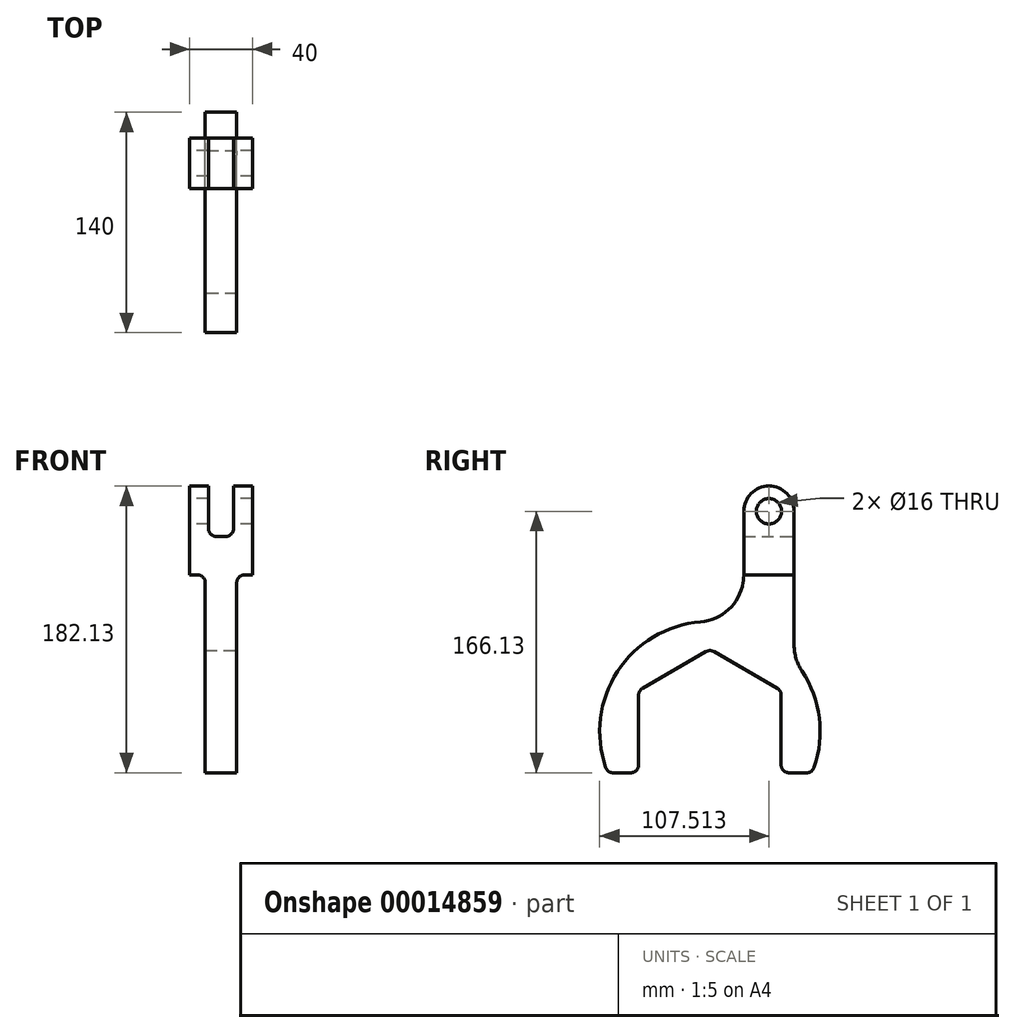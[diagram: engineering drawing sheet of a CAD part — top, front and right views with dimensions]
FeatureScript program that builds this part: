
annotation { "Feature Type Name" : "Feature", "Feature Type Description" : "" }
export const myFeature = defineFeature(function(context is Context, id is Id, definition is map)
    precondition{}
    {
        {
            var Q0;
            Q0=qCreatedBy(makeId("Right.planeOp"),FACE);
            var sketch = newSketch(context, id + "F0", { "sketchPlane" : qUnion([Q0])});
            skCircle(sketch, "E0.cCircle", {"center": v(0, 0) * mm, "radius": 45.25 * mm, "construction": true});
            skLineSegment(sketch, "E0.0", {"start": v(-45.25, -26.13) * mm, "end": v(-45.25, 26.13) * mm});
            skLineSegment(sketch, "E0.1", {"start": v(-45.25, 26.13) * mm, "end": v(0, 52.25) * mm});
            skLineSegment(sketch, "E0.2", {"start": v(0, 52.25) * mm, "end": v(45.25, 26.13) * mm});
            skLineSegment(sketch, "E0.3", {"start": v(45.25, 26.13) * mm, "end": v(45.25, -26.13) * mm});
            skLineSegment(sketch, "E0.4", {"start": v(22.63, -39.19) * mm, "end": v(21.51, -39.83) * mm});
            skPoint(sketch, "E0.0.midPoint", {"position": v(-45.25, 0) * mm});
            skLineSegment(sketch, "E1", {"start": v(0, 0) * mm, "end": v(0, 140) * mm, "construction": true});
            skLineSegment(sketch, "E2", {"start": v(0, 140) * mm, "end": v(132.53, 140) * mm, "construction": true});
            skLineSegment(sketch, "E3", {"start": v(0, 0) * mm, "end": v(37.51, 140) * mm, "construction": true});
            skCircle(sketch, "E4", {"center": v(37.51, 140) * mm, "radius": 8 * mm});
            skArc(sketch, "E5", {"start": v(53.51, 140) * mm, "mid": v(37.51, 156) * mm, "end": v(21.51, 140) * mm});
            skLineSegment(sketch, "E6", {"start": v(53.51, 140) * mm, "end": v(53.51, 55) * mm});
            skArc(sketch, "E7", {"start": v(64.94, -26.13) * mm, "mid": v(69.65, 6.99) * mm, "end": v(58.46, 38.5) * mm});
            skLineSegment(sketch, "E8", {"start": v(37.51, 140) * mm, "end": v(37.51, 210.9) * mm, "construction": true});
            skLineSegment(sketch, "E9.0.MirrorCS", {"start": v(21.51, 140) * mm, "end": v(21.51, 99.64) * mm});
            skLineSegment(sketch, "E10", {"start": v(-64.94, -26.13) * mm, "end": v(-45.25, -26.13) * mm});
            skPoint(sketch, "E11.orphan", {"position": v(53.51, -53.76) * mm});
            skArc(sketch, "E12.trimOffspring", {"start": v(-5.94, 69.75) * mm, "mid": v(-59.62, 36.69) * mm, "end": v(-64.94, -26.13) * mm});
            skPoint(sketch, "E13.orphan", {"position": v(-113.23, -26.13) * mm});
            skLineSegment(sketch, "E14.trimOffspring", {"start": v(45.25, -26.13) * mm, "end": v(64.94, -26.13) * mm});
            skPoint(sketch, "E15.visualSharp", {"position": v(53.51, 45.13) * mm});
            skArc(sketch, "E15.filletArc", {"start": v(53.51, 55) * mm, "mid": v(54.78, 46.4) * mm, "end": v(58.46, 38.5) * mm});
            skPoint(sketch, "E16.newPointA", {"position": v(21.51, -53.76) * mm});
            skArc(sketch, "E16.filletArc", {"start": v(-5.94, 69.75) * mm, "mid": v(13.6, 79.35) * mm, "end": v(21.51, 99.64) * mm});
            skSolve(sketch);
        }
        {
            var Q0;
            Q0=qSketchRegion(id+"F0",true);
            extrude(context, id + "F1", {"entities" : qUnion([Q0]), "endBound" : BoundingType.SYMMETRIC, "depth" : 40 * mm});
        }
        {
            var Q0;
            Q0=makeQuery(id+"F1.opExtrude","CAP_FACE",FACE,{"disambiguationData":[OSD([sQuery(id+"F0.wireOp",EDGE,"E0.0"),sQuery(id+"F0.wireOp",EDGE,"E0.1"),sQuery(id+"F0.wireOp",EDGE,"E0.2"),sQuery(id+"F0.wireOp",EDGE,"E0.3"),sQuery(id+"F0.wireOp",EDGE,"E4"),sQuery(id+"F0.wireOp",EDGE,"E5"),sQuery(id+"F0.wireOp",EDGE,"E6"),sQuery(id+"F0.wireOp",EDGE,"E7"),sQuery(id+"F0.wireOp",EDGE,"E9.0.MirrorCS"),sQuery(id+"F0.wireOp",EDGE,"E10"),sQuery(id+"F0.wireOp",EDGE,"E12.trimOffspring"),sQuery(id+"F0.wireOp",EDGE,"E14.trimOffspring"),sQuery(id+"F0.wireOp",EDGE,"E15.filletArc"),sQuery(id+"F0.wireOp",EDGE,"E16.filletArc")])],"isStart":false});
            var sketch = newSketch(context, id + "F2", { "sketchPlane" : qUnion([Q0])});
            skArc(sketch, "E17.0", {"start": v(-5.94, 69.75) * mm, "mid": v(-59.62, 36.69) * mm, "end": v(-64.94, -26.13) * mm});
            skLineSegment(sketch, "E18.0", {"start": v(-64.94, -26.13) * mm, "end": v(-45.25, -26.13) * mm});
            skLineSegment(sketch, "E19.0", {"start": v(-45.25, -26.13) * mm, "end": v(-45.25, 26.13) * mm});
            skLineSegment(sketch, "E20.0", {"start": v(-45.25, 26.13) * mm, "end": v(0, 52.25) * mm});
            skLineSegment(sketch, "E21.0", {"start": v(0, 52.25) * mm, "end": v(45.25, 26.13) * mm});
            skLineSegment(sketch, "E22.0", {"start": v(45.25, 26.13) * mm, "end": v(45.25, -26.13) * mm});
            skLineSegment(sketch, "E23.0", {"start": v(45.25, -26.13) * mm, "end": v(64.94, -26.13) * mm});
            skArc(sketch, "E24.0", {"start": v(64.94, -26.13) * mm, "mid": v(69.65, 6.99) * mm, "end": v(58.46, 38.5) * mm});
            skArc(sketch, "E25.0", {"start": v(53.51, 55) * mm, "mid": v(54.78, 46.4) * mm, "end": v(58.46, 38.5) * mm});
            skArc(sketch, "E26.0", {"start": v(-5.94, 69.75) * mm, "mid": v(13.6, 79.35) * mm, "end": v(21.51, 99.64) * mm});
            skLineSegment(sketch, "E27.0", {"start": v(53.51, 140) * mm, "end": v(53.51, 55) * mm});
            skLineSegment(sketch, "E28", {"start": v(21.51, 99.64) * mm, "end": v(67.54, 99.64) * mm});
            skSolve(sketch);
        }
        {
            var Q0;
            Q0=qSketchRegion(id+"F2",true);
            extrude(context, id + "F3", {"entities" : qUnion([Q0]), "operationType" : NewBodyOperationType.REMOVE, "oppositeDirection" : true, "depth" : 10 * mm});
        }
        {
            var Q0;
            Q0=makeQuery(id+"F1.opExtrude","CAP_FACE",FACE,{"disambiguationData":[OSD([sQuery(id+"F0.wireOp",EDGE,"E0.0"),sQuery(id+"F0.wireOp",EDGE,"E0.1"),sQuery(id+"F0.wireOp",EDGE,"E0.2"),sQuery(id+"F0.wireOp",EDGE,"E0.3"),sQuery(id+"F0.wireOp",EDGE,"E4"),sQuery(id+"F0.wireOp",EDGE,"E5"),sQuery(id+"F0.wireOp",EDGE,"E6"),sQuery(id+"F0.wireOp",EDGE,"E7"),sQuery(id+"F0.wireOp",EDGE,"E9.0.MirrorCS"),sQuery(id+"F0.wireOp",EDGE,"E10"),sQuery(id+"F0.wireOp",EDGE,"E12.trimOffspring"),sQuery(id+"F0.wireOp",EDGE,"E14.trimOffspring"),sQuery(id+"F0.wireOp",EDGE,"E15.filletArc"),sQuery(id+"F0.wireOp",EDGE,"E16.filletArc")])],"isStart":true});
            var sketch = newSketch(context, id + "F4", { "sketchPlane" : qUnion([Q0])});
            skArc(sketch, "E29.0", {"start": v(5.94, 69.75) * mm, "mid": v(-13.6, 79.35) * mm, "end": v(-21.51, 99.64) * mm});
            skLineSegment(sketch, "E30.0", {"start": v(-21.51, 99.64) * mm, "end": v(-53.51, 99.64) * mm});
            skLineSegment(sketch, "E31.0", {"start": v(-53.51, 140) * mm, "end": v(-53.51, 55) * mm});
            skArc(sketch, "E32.0", {"start": v(-53.51, 55) * mm, "mid": v(-54.78, 46.4) * mm, "end": v(-58.46, 38.5) * mm});
            skArc(sketch, "E33.0", {"start": v(-64.94, -26.13) * mm, "mid": v(-69.65, 6.99) * mm, "end": v(-58.46, 38.5) * mm});
            skLineSegment(sketch, "E34.0", {"start": v(-45.25, -26.13) * mm, "end": v(-64.94, -26.13) * mm});
            skLineSegment(sketch, "E35.0", {"start": v(-45.25, 26.13) * mm, "end": v(-45.25, -26.13) * mm});
            skLineSegment(sketch, "E36.0", {"start": v(0, 52.25) * mm, "end": v(-45.25, 26.13) * mm});
            skLineSegment(sketch, "E37.0", {"start": v(45.25, 26.13) * mm, "end": v(0, 52.25) * mm});
            skLineSegment(sketch, "E38.0", {"start": v(45.25, -26.13) * mm, "end": v(45.25, 26.13) * mm});
            skLineSegment(sketch, "E39.0", {"start": v(64.94, -26.13) * mm, "end": v(45.25, -26.13) * mm});
            skArc(sketch, "E40.0", {"start": v(5.94, 69.75) * mm, "mid": v(59.62, 36.69) * mm, "end": v(64.94, -26.13) * mm});
            skSolve(sketch);
        }
        {
            var Q0;
            Q0=qSketchRegion(id+"F4",true);
            extrude(context, id + "F5", {"entities" : qUnion([Q0]), "operationType" : NewBodyOperationType.REMOVE, "oppositeDirection" : true, "depth" : 10 * mm});
        }
        {
            var Q0;
            Q0=makeQuery(id+"F5.boolean.opBoolean","COPY",EDGE,{"derivedFrom":makeQuery(id+"F5.opExtrude","CAP_EDGE",EDGE,{"disambiguationData":[OSD([sQuery(id+"F4.wireOp",EDGE,"E30.0")])],"isStart":false})});
            var Q1;
            Q1=makeQuery(id+"F5.boolean.opBoolean","COPY",EDGE,{"derivedFrom":makeQuery(id+"F5.opExtrude","CAP_EDGE",EDGE,{"disambiguationData":[OSD([sQuery(id+"F4.wireOp",EDGE,"E30.0")])],"isStart":true})});
            var Q2;
            Q2=makeQuery(id+"F3.boolean.opBoolean","COPY",EDGE,{"derivedFrom":makeQuery(id+"F3.opExtrude","CAP_EDGE",EDGE,{"disambiguationData":[OSD([sQuery(id+"F2.wireOp",EDGE,"E28")])],"isStart":false})});
            var Q3;
            Q3=makeQuery(id+"F3.boolean.opBoolean","COPY",EDGE,{"derivedFrom":makeQuery(id+"F3.opExtrude","CAP_EDGE",EDGE,{"disambiguationData":[OSD([sQuery(id+"F2.wireOp",EDGE,"E28")])],"isStart":true})});
            fillet(context, id + "F6", {"entities" : qUnion([Q0, Q1, Q2, Q3]), "radius" : 5 * mm, "tangentPropagation" : true, "allowEdgeOverflow" : false});
        }
        {
            var Q0;
            Q0=makeQuery(id+"F1.opExtrude","SWEPT_EDGE",EDGE,{"disambiguationData":[OSD([sQuery(id+"F0.wireOp",EDGE,"E0.3"),sQuery(id+"F0.wireOp",EDGE,"E14.trimOffspring")])]});
            var Q1;
            Q1=makeQuery(id+"F1.opExtrude","SWEPT_EDGE",EDGE,{"disambiguationData":[OSD([sQuery(id+"F0.wireOp",EDGE,"E0.0"),sQuery(id+"F0.wireOp",EDGE,"E10")])]});
            var Q2;
            Q2=makeQuery(id+"F1.opExtrude","SWEPT_EDGE",EDGE,{"disambiguationData":[OSD([sQuery(id+"F0.wireOp",EDGE,"E10"),sQuery(id+"F0.wireOp",EDGE,"E12.trimOffspring")])]});
            var Q3;
            Q3=makeQuery(id+"F1.opExtrude","SWEPT_EDGE",EDGE,{"disambiguationData":[OSD([sQuery(id+"F0.wireOp",EDGE,"E7"),sQuery(id+"F0.wireOp",EDGE,"E14.trimOffspring")])]});
            fillet(context, id + "F7", {"entities" : qUnion([Q0, Q1, Q2, Q3]), "radius" : 5 * mm, "tangentPropagation" : true, "allowEdgeOverflow" : false});
        }
        {
            var Q0;
            Q0=makeQuery(id+"F1.opExtrude","SWEPT_EDGE",EDGE,{"disambiguationData":[OSD([sQuery(id+"F0.wireOp",EDGE,"E0.2"),sQuery(id+"F0.wireOp",EDGE,"E0.3")])]});
            var Q1;
            Q1=makeQuery(id+"F1.opExtrude","SWEPT_EDGE",EDGE,{"disambiguationData":[OSD([sQuery(id+"F0.wireOp",EDGE,"E0.1"),sQuery(id+"F0.wireOp",EDGE,"E0.2")])]});
            var Q2;
            Q2=makeQuery(id+"F1.opExtrude","SWEPT_EDGE",EDGE,{"disambiguationData":[OSD([sQuery(id+"F0.wireOp",EDGE,"E0.0"),sQuery(id+"F0.wireOp",EDGE,"E0.1")])]});
            fillet(context, id + "F8", {"entities" : qUnion([Q0, Q1, Q2]), "radius" : 5 * mm, "tangentPropagation" : true, "allowEdgeOverflow" : false});
        }
        {
            var Q0;
            Q0=makeQuery(id+"F1.opExtrude","SWEPT_FACE",FACE,{"disambiguationData":[OSD([sQuery(id+"F0.wireOp",EDGE,"E6")])]});
            var sketch = newSketch(context, id + "F9", { "sketchPlane" : qUnion([Q0])});
            skLineSegment(sketch, "E41", {"start": v(0, 181.36) * mm, "end": v(0, -58.54) * mm, "construction": true});
            skLineSegment(sketch, "E42", {"start": v(-20, 156) * mm, "end": v(20, 156) * mm, "construction": true});
            skLineSegment(sketch, "E43.0", {"start": v(-20, 140) * mm, "end": v(20, 140) * mm, "construction": true});
            skLineSegment(sketch, "E44.0.MirrorCS", {"start": v(-20, 124) * mm, "end": v(20, 124) * mm, "construction": true});
            skLineSegment(sketch, "E45.0", {"start": v(-8, 181.36) * mm, "end": v(-8, -58.54) * mm, "construction": true});
            skLineSegment(sketch, "E46.0.MirrorCS", {"start": v(8, 181.36) * mm, "end": v(8, -58.54) * mm, "construction": true});
            skLineSegment(sketch, "E47.bottom", {"start": v(-8, 181.36) * mm, "end": v(8, 181.36) * mm});
            skLineSegment(sketch, "E47.top", {"start": v(-8, 124) * mm, "end": v(8, 124) * mm});
            skLineSegment(sketch, "E47.left", {"start": v(-8, 181.36) * mm, "end": v(-8, 124) * mm});
            skLineSegment(sketch, "E47.right", {"start": v(8, 181.36) * mm, "end": v(8, 124) * mm});
            skSolve(sketch);
        }
        {
            var Q0;
            Q0=qSketchRegion(id+"F9",true);
            extrude(context, id + "F10", {"entities" : qUnion([Q0]), "operationType" : NewBodyOperationType.REMOVE, "endBound" : BoundingType.THROUGH_ALL, "oppositeDirection" : true, "depth" : 25 * mm});
        }
        {
            var Q0;
            Q0=makeQuery(id+"F10.boolean.opBoolean","COPY",EDGE,{"derivedFrom":makeQuery(id+"F10.opExtrude","SWEPT_EDGE",EDGE,{"disambiguationData":[OSD([sQuery(id+"F9.wireOp",EDGE,"E47.top"),sQuery(id+"F9.wireOp",EDGE,"E47.left")])]})});
            var Q1;
            Q1=makeQuery(id+"F10.boolean.opBoolean","COPY",EDGE,{"derivedFrom":makeQuery(id+"F10.opExtrude","SWEPT_EDGE",EDGE,{"disambiguationData":[OSD([sQuery(id+"F9.wireOp",EDGE,"E47.top"),sQuery(id+"F9.wireOp",EDGE,"E47.right")])]})});
            fillet(context, id + "F11", {"entities" : qUnion([Q0, Q1]), "radius" : 5 * mm, "tangentPropagation" : true, "allowEdgeOverflow" : false});
        }
    });
